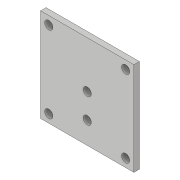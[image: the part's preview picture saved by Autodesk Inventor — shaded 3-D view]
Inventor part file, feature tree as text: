
AUTODESK INVENTOR PART (.ipt)
format: ipt  version: 2019 (Build 230136000, 136)  size: 112,128 bytes
history: native  units: mm
features: extrude x4, sketch x4
ambient origin geometry x8: Origin, YZ Plane, XZ Plane, XY Plane, X Axis, Y Axis, Z Axis, Center Point
bodies: Solid1 (feature_tree)
feature tree (8):
  extrude  "Extrusion1"  Depth=170.0mm
  extrude  "Extrusion2"  Depth=10.0mm
  extrude  "Extrusion3"  Depth=155.0mm
  extrude  "Extrusion4"  Depth=10.0mm
  sketch  "Sketch1"  dims[d0=170.0mm d1=170.0mm]
  sketch  "Sketch2"  dims[d2=10.0mm d3=0.0mm d4=15.0mm]
  sketch  "Sketch3"  dims[d5=15.0mm d6=155.0mm]
  sketch  "Sketch4"  dims[d7=140.0mm d8=140.0mm d9=140.0mm d10=15.0mm d11=15.0mm d12=15.0mm d13=15.0mm d14=10.0mm d15=0.0mm d16=85.0mm d17=85.0mm d18=15.0mm d19=10.0mm d20=0.0mm d21=85.0mm d22=40.0mm d23=15.0mm d24=10.0mm d25=0.0mm]
